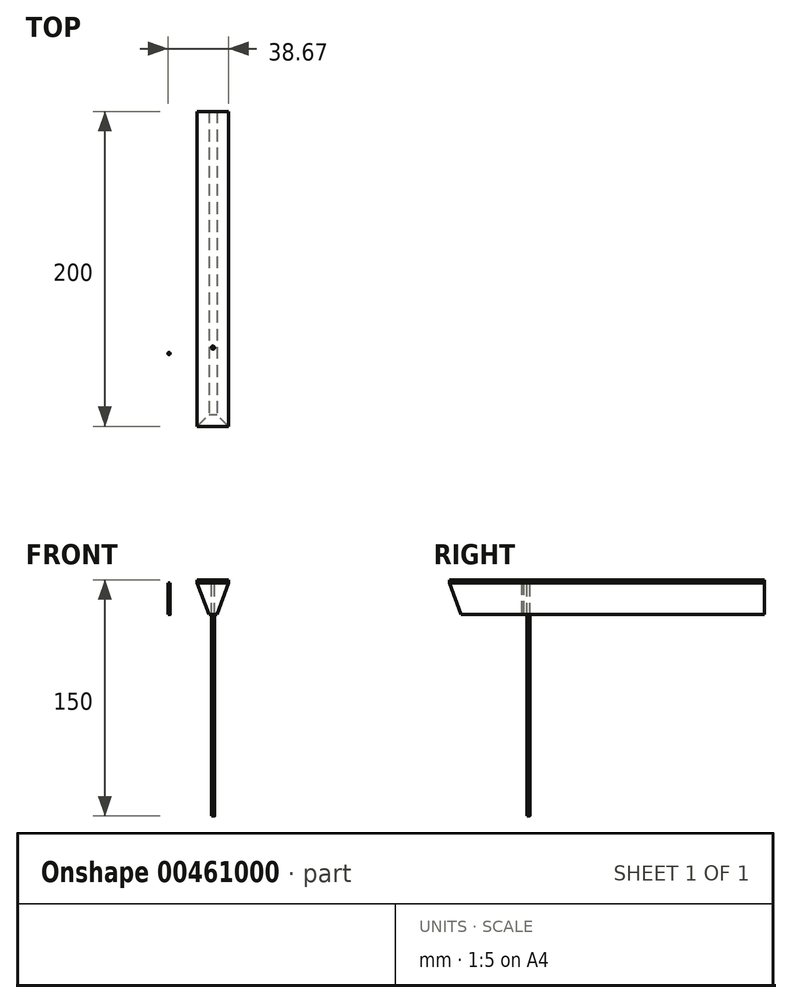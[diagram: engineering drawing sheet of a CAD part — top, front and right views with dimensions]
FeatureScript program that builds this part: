
annotation { "Feature Type Name" : "Feature", "Feature Type Description" : "" }
export const myFeature = defineFeature(function(context is Context, id is Id, definition is map)
    precondition{}
    {
        {
            var Q0;
            Q0=qCreatedBy(makeId("Top.planeOp"),FACE);
            var sketch = newSketch(context, id + "F0", { "sketchPlane" : qUnion([Q0])});
            skLineSegment(sketch, "E0.bottom", {"start": v(0, 0) * mm, "end": v(20, 0) * mm});
            skLineSegment(sketch, "E0.top", {"start": v(0, 200) * mm, "end": v(20, 200) * mm});
            skLineSegment(sketch, "E0.left", {"start": v(0, 0) * mm, "end": v(0, 200) * mm});
            skLineSegment(sketch, "E0.right", {"start": v(20, 0) * mm, "end": v(20, 200) * mm});
            skSolve(sketch);
        }
        {
            var Q0;
            Q0 = qSketchRegion(id + "F0", true);
            extrude(context, id + "F1", {"entities" : qUnion([Q0]), "depth" : 20 * mm});
        }
        {
            var Q0;
            Q0=makeQuery(id+"F1.opExtrude","SWEPT_FACE",FACE,{"disambiguationData":[OSD([sQuery(id+"F0.wireOp",EDGE,"E0.bottom")])]});
            var sketch = newSketch(context, id + "F2", { "sketchPlane" : qUnion([Q0])});
            skLineSegment(sketch, "E1", {"start": v(0, 20) * mm, "end": v(7.5, 0) * mm});
            skLineSegment(sketch, "E2", {"start": v(7.5, 0) * mm, "end": v(0, 0) * mm});
            skLineSegment(sketch, "E3", {"start": v(0, 0) * mm, "end": v(0, 20) * mm});
            skLineSegment(sketch, "E4", {"start": v(12.5, 0) * mm, "end": v(20, 0) * mm});
            skLineSegment(sketch, "E5", {"start": v(20, 0) * mm, "end": v(20, 20) * mm});
            skLineSegment(sketch, "E6", {"start": v(20, 20) * mm, "end": v(12.5, 0) * mm});
            skSolve(sketch);
        }
        {
            var Q0;
            Q0 = qSketchRegion(id + "F2", true);
            extrude(context, id + "F3", {"entities" : qUnion([Q0]), "operationType" : NewBodyOperationType.REMOVE, "endBound" : BoundingType.THROUGH_ALL, "oppositeDirection" : true, "depth" : 25 * mm});
        }
        {
            var Q0;
            Q0=qCreatedBy(makeId("Right.planeOp"),FACE);
            var sketch = newSketch(context, id + "F4", { "sketchPlane" : qUnion([Q0])});
            skLineSegment(sketch, "E7", {"start": v(0, 0) * mm, "end": v(0, 20) * mm});
            skLineSegment(sketch, "E8", {"start": v(0, 20) * mm, "end": v(7.28, 0) * mm});
            skLineSegment(sketch, "E9", {"start": v(7.28, 0) * mm, "end": v(0, 0) * mm});
            skSolve(sketch);
        }
        {
            var Q0;
            Q0 = qSketchRegion(id + "F4", true);
            extrude(context, id + "F5", {"entities" : qUnion([Q0]), "operationType" : NewBodyOperationType.REMOVE, "endBound" : BoundingType.THROUGH_ALL, "depth" : 25 * mm});
        }
        {
            var Q0;
            Q0=makeQuery(id+"F1.opExtrude","CAP_FACE",FACE,{"disambiguationData":[OSD([sQuery(id+"F0.wireOp",EDGE,"E0.bottom"),sQuery(id+"F0.wireOp",EDGE,"E0.top"),sQuery(id+"F0.wireOp",EDGE,"E0.left"),sQuery(id+"F0.wireOp",EDGE,"E0.right")])],"isStart":false});
            var sketch = newSketch(context, id + "F6", { "sketchPlane" : qUnion([Q0])});
            skLineSegment(sketch, "E10.bottom", {"start": v(0, 0) * mm, "end": v(20, 0) * mm});
            skLineSegment(sketch, "E10.top", {"start": v(0, 200) * mm, "end": v(20, 200) * mm});
            skLineSegment(sketch, "E10.left", {"start": v(0, 0) * mm, "end": v(0, 200) * mm});
            skLineSegment(sketch, "E10.right", {"start": v(20, 0) * mm, "end": v(20, 200) * mm});
            skSolve(sketch);
        }
        {
            var Q0;
            Q0 = qSketchRegion(id + "F6", true);
            extrude(context, id + "F7", {"entities" : qUnion([Q0]), "depth" : 2 * mm});
        }
        {
            var Q0;
            Q0=makeQuery(id+"F7.opExtrude","CAP_FACE",FACE,{"disambiguationData":[OSD([sQuery(id+"F6.wireOp",EDGE,"E10.bottom"),sQuery(id+"F6.wireOp",EDGE,"E10.top"),sQuery(id+"F6.wireOp",EDGE,"E10.left"),sQuery(id+"F6.wireOp",EDGE,"E10.right")])],"isStart":false});
            var sketch = newSketch(context, id + "F8", { "sketchPlane" : qUnion([Q0])});
            skCircle(sketch, "E11", {"center": v(10, 50) * mm, "radius": 1 * mm});
            skSolve(sketch);
        }
        {
            var Q0;
            Q0 = qSketchRegion(id + "F8", true);
            extrude(context, id + "F9", {"entities" : qUnion([Q0]), "oppositeDirection" : true, "depth" : 150 * mm});
        }
        {
            var Q0;
            Q0=qCreatedBy(makeId("Top.planeOp"),FACE);
            var sketch = newSketch(context, id + "F10", { "sketchPlane" : qUnion([Q0])});
            skCircle(sketch, "E12", {"center": v(-17.92, 46.27) * mm, "radius": 0.75 * mm});
            skSolve(sketch);
        }
        {
            var Q0;
            Q0 = qSketchRegion(id + "F10", true);
            extrude(context, id + "F11", {"entities" : qUnion([Q0]), "depth" : 20 * mm});
        }
    });
